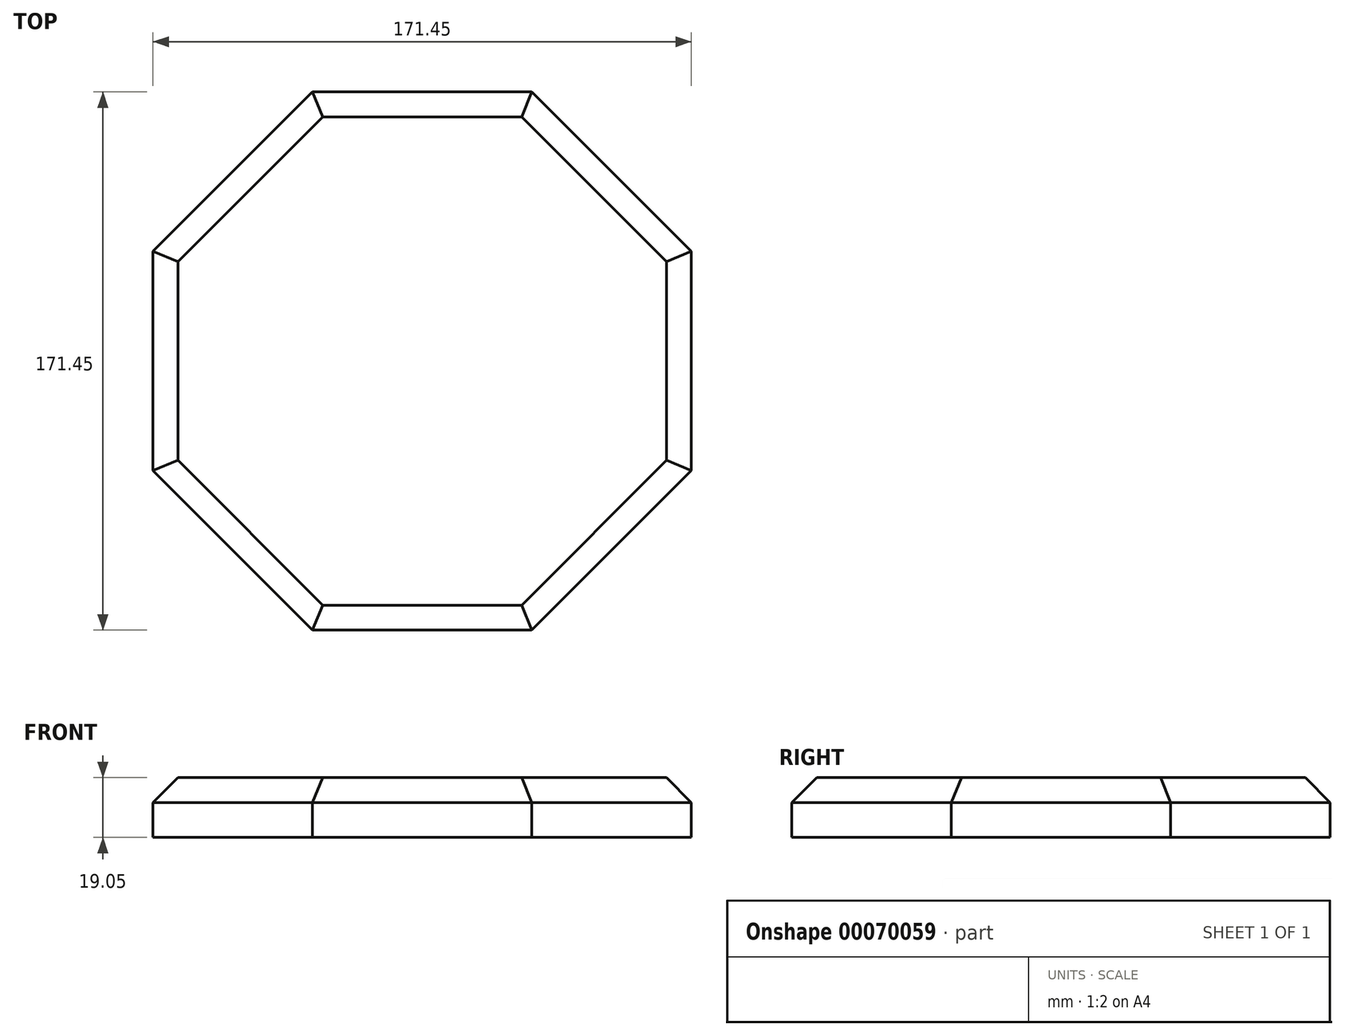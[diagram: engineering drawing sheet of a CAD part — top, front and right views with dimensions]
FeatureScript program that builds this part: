
annotation { "Feature Type Name" : "Feature", "Feature Type Description" : "" }
export const myFeature = defineFeature(function(context is Context, id is Id, definition is map)
    precondition{}
    {
        {
            var Q0;
            Q0=qCreatedBy(makeId("Top.planeOp"),FACE);
            var sketch = newSketch(context, id + "F0", { "sketchPlane" : qUnion([Q0])});
            skLineSegment(sketch, "E0.bottom", {"start": v(-85.73, 85.73) * mm, "end": v(85.73, 85.73) * mm});
            skLineSegment(sketch, "E0.top", {"start": v(-85.73, -85.73) * mm, "end": v(85.73, -85.73) * mm});
            skLineSegment(sketch, "E0.left", {"start": v(-85.73, 85.73) * mm, "end": v(-85.73, -85.73) * mm});
            skLineSegment(sketch, "E0.right", {"start": v(85.73, 85.73) * mm, "end": v(85.73, -85.73) * mm});
            skSolve(sketch);
        }
        {
            var Q0;
            Q0=makeQuery(id+"F0.imprint","IMPRINT",FACE,{"disambiguationData":[TD([[makeQuery(id+"F0.imprint","IMPRINT",EDGE,{"derivedFrom":sQuery(id+"F0.wireOp",EDGE,"E0.bottom")}),-1.0]])]});
            extrude(context, id + "F1", {"entities" : qUnion([Q0]), "depth" : 19.05 * mm});
        }
        {
            var Q0;
            Q0=makeQuery(id+"F1.opExtrude","CAP_FACE",FACE,{"disambiguationData":[OSD([sQuery(id+"F0.wireOp",EDGE,"E0.bottom"),sQuery(id+"F0.wireOp",EDGE,"E0.top"),sQuery(id+"F0.wireOp",EDGE,"E0.left"),sQuery(id+"F0.wireOp",EDGE,"E0.right"),sQuery(id+"F0.wireOp",EDGE,"989e4ac2-cbae-46ec-ac43-b30b8cb76129"),sQuery(id+"F0.wireOp",EDGE,"f01b9872-5823-4ad4-8aaf-3aa102a647f4"),sQuery(id+"F0.wireOp",EDGE,"f254082f-be6d-486d-81c3-8d4d65e6b824"),sQuery(id+"F0.wireOp",EDGE,"21b5d828-52df-4a59-b6f1-21bcb8ec3c0c"),sQuery(id+"F0.wireOp",EDGE,"d4020edf-602f-45da-a7a3-b06696fa117d"),sQuery(id+"F0.wireOp",EDGE,"905035b1-59ca-4ffc-a016-3912243c06da"),sQuery(id+"F0.wireOp",EDGE,"2c110506-1446-466a-9127-3dc12a78b58e"),sQuery(id+"F0.wireOp",EDGE,"26ce887d-3531-4269-9341-2fdd4bb3d620"),sQuery(id+"F0.wireOp",EDGE,"475ccb10-8f8e-49a7-93a4-93c3f0626b4c.bottom"),sQuery(id+"F0.wireOp",EDGE,"475ccb10-8f8e-49a7-93a4-93c3f0626b4c.top"),sQuery(id+"F0.wireOp",EDGE,"475ccb10-8f8e-49a7-93a4-93c3f0626b4c.left"),sQuery(id+"F0.wireOp",EDGE,"475ccb10-8f8e-49a7-93a4-93c3f0626b4c.right"),sQuery(id+"F0.wireOp",EDGE,"8ed021d0-fdce-44df-976c-de6f7beabc6d"),sQuery(id+"F0.wireOp",EDGE,"05c30dd9-ea8d-42c8-9be9-557685326a9e"),sQuery(id+"F0.wireOp",EDGE,"c46a8fb0-1c3f-46cc-903a-dbb448825e2e"),sQuery(id+"F0.wireOp",EDGE,"583893c2-0e6e-4aff-a0bb-19d91ca0a52e"),sQuery(id+"F0.wireOp",EDGE,"14300feb-ca35-44da-9651-15a41913f3c9.0"),sQuery(id+"F0.wireOp",EDGE,"8128e34a-8f59-4c2e-8099-998957f98d7b.0"),sQuery(id+"F0.wireOp",EDGE,"95882136-e9e6-4eb0-a4c0-31bc3ca21f6b.0"),sQuery(id+"F0.wireOp",EDGE,"ec29514e-9971-47f8-95a7-5a5ba83320e9.0")])],"isStart":false});
            var sketch = newSketch(context, id + "F2", { "sketchPlane" : qUnion([Q0])});
            skLineSegment(sketch, "E1", {"start": v(7.95, -33.34) * mm, "end": v(7.95, -20.64) * mm});
            skLineSegment(sketch, "E2", {"start": v(-33.34, 7.94) * mm, "end": v(-20.64, 7.94) * mm});
            skLineSegment(sketch, "E3", {"start": v(-20.64, -7.94) * mm, "end": v(-33.34, -7.94) * mm});
            skLineSegment(sketch, "E4", {"start": v(33.34, -9.24) * mm, "end": v(20.64, -9.24) * mm});
            skLineSegment(sketch, "E5.trimOffspring", {"start": v(-7.72, 33.34) * mm, "end": v(-7.8, 20.64) * mm});
            skPoint(sketch, "E6.center.orphan", {"position": v(0, -1.3) * mm});
            skLineSegment(sketch, "E7", {"start": v(-33.34, -7.94) * mm, "end": v(-33.34, 7.94) * mm});
            skLineSegment(sketch, "E8", {"start": v(33.34, -9.24) * mm, "end": v(33.34, 7.94) * mm});
            skPoint(sketch, "E8.startSnap0", {"position": v(33.34, -9.24) * mm});
            skLineSegment(sketch, "E9", {"start": v(-8.18, -33.34) * mm, "end": v(7.95, -33.34) * mm});
            skPoint(sketch, "E10.orphan", {"position": v(0, 20.64) * mm});
            skPoint(sketch, "E11.orphan", {"position": v(33.34, -6.04) * mm});
            skPoint(sketch, "E12.orphan", {"position": v(20.64, 0) * mm});
            skPoint(sketch, "E13.orphan", {"position": v(0, -20.64) * mm});
            skLineSegment(sketch, "E14.trimOffspring", {"start": v(20.64, 20.64) * mm, "end": v(20.64, 20.75) * mm});
            skPoint(sketch, "E15.orphan", {"position": v(-20.64, 0) * mm});
            skLineSegment(sketch, "E16.trimOffspring", {"start": v(20.75, 20.64) * mm, "end": v(20.64, 20.75) * mm});
            skLineSegment(sketch, "E17", {"start": v(-20.64, -7.94) * mm, "end": v(-8.1, -20.64) * mm});
            skLineSegment(sketch, "E18", {"start": v(20.64, -9.24) * mm, "end": v(7.95, -20.64) * mm});
            skLineSegment(sketch, "E19", {"start": v(-7.8, 20.64) * mm, "end": v(-20.64, 7.94) * mm});
            skLineSegment(sketch, "E20", {"start": v(-7.72, 33.34) * mm, "end": v(7.95, 33.34) * mm});
            skLineSegment(sketch, "E21", {"start": v(20.64, 7.94) * mm, "end": v(7.95, 20.64) * mm});
            skLineSegment(sketch, "E22.trimOffspring", {"start": v(20.64, 20.64) * mm, "end": v(20.75, 20.64) * mm});
            skLineSegment(sketch, "E23.trimOffspring", {"start": v(20.64, 7.94) * mm, "end": v(33.34, 7.94) * mm});
            skLineSegment(sketch, "E24.trimOffspring", {"start": v(-8.1, -20.64) * mm, "end": v(-8.18, -33.34) * mm});
            skLineSegment(sketch, "E25.trimOffspring", {"start": v(7.95, 20.64) * mm, "end": v(7.95, 33.34) * mm});
            skLineSegment(sketch, "E26", {"start": v(20.64, -9.24) * mm, "end": v(20.64, 7.94) * mm});
            skLineSegment(sketch, "E27", {"start": v(-20.64, -7.94) * mm, "end": v(-20.64, 7.94) * mm});
            skLineSegment(sketch, "E28", {"start": v(-7.8, 20.64) * mm, "end": v(7.95, 20.64) * mm});
            skLineSegment(sketch, "E29", {"start": v(-8.1, -20.64) * mm, "end": v(7.95, -20.64) * mm});
            skSolve(sketch);
        }
        {
            var Q0;
            Q0=makeQuery(id+"F2.imprint","IMPRINT",FACE,{"disambiguationData":[TD([[makeQuery(id+"F2.imprint","IMPRINT",EDGE,{"derivedFrom":sQuery(id+"F2.wireOp",EDGE,"E17")}),1.0]])]});
            extrude(context, id + "F3", {"entities" : qUnion([Q0]), "depth" : 127 * mm});
        }
        {
            var Q0;
            Q0=makeQuery(id+"F2.imprint","IMPRINT",FACE,{"disambiguationData":[TD([[makeQuery(id+"F2.imprint","IMPRINT",EDGE,{"derivedFrom":sQuery(id+"F2.wireOp",EDGE,"E4")}),-1.0]])]});
            extrude(context, id + "F4", {"entities" : qUnion([Q0]), "depth" : 203.2 * mm});
        }
        {
            var Q0;
            Q0=makeQuery(id+"F4.opExtrude","CAP_EDGE",EDGE,{"disambiguationData":[OSD([sQuery(id+"F2.wireOp",EDGE,"E8")])],"isStart":false});
            chamfer(context, id + "F5", {"entities" : qUnion([Q0]), "width" : 5.08 * mm, "tangentPropagation" : true});
        }
        {
            var Q0;
            Q0=makeQuery(id+"F2.imprint","IMPRINT",FACE,{"disambiguationData":[TD([[makeQuery(id+"F2.imprint","IMPRINT",EDGE,{"derivedFrom":sQuery(id+"F2.wireOp",EDGE,"E1")}),1.0]])]});
            extrude(context, id + "F6", {"entities" : qUnion([Q0]), "depth" : 177.8 * mm});
        }
        {
            var Q0;
            Q0=makeQuery(id+"F6.opExtrude","CAP_EDGE",EDGE,{"disambiguationData":[OSD([sQuery(id+"F2.wireOp",EDGE,"E9")])],"isStart":false});
            chamfer(context, id + "F7", {"entities" : qUnion([Q0]), "width" : 5.08 * mm, "tangentPropagation" : true});
        }
        {
            var Q0;
            Q0=makeQuery(id+"F2.imprint","IMPRINT",FACE,{"disambiguationData":[TD([[makeQuery(id+"F2.imprint","IMPRINT",EDGE,{"derivedFrom":sQuery(id+"F2.wireOp",EDGE,"E5.trimOffspring")}),1.0]])]});
            extrude(context, id + "F8", {"entities" : qUnion([Q0]), "depth" : 177.8 * mm});
        }
        {
            var Q0;
            Q0=makeQuery(id+"F8.opExtrude","CAP_EDGE",EDGE,{"disambiguationData":[OSD([sQuery(id+"F2.wireOp",EDGE,"E20")])],"isStart":false});
            chamfer(context, id + "F9", {"entities" : qUnion([Q0]), "width" : 5.08 * mm, "tangentPropagation" : true});
        }
        {
            var Q0;
            Q0=makeQuery(id+"F2.imprint","IMPRINT",FACE,{"disambiguationData":[TD([[makeQuery(id+"F2.imprint","IMPRINT",EDGE,{"derivedFrom":sQuery(id+"F2.wireOp",EDGE,"E2")}),-1.0]])]});
            extrude(context, id + "F10", {"entities" : qUnion([Q0]), "depth" : 152.4 * mm});
        }
        {
            var Q0;
            Q0=makeQuery(id+"F10.opExtrude","CAP_EDGE",EDGE,{"disambiguationData":[OSD([sQuery(id+"F2.wireOp",EDGE,"E7")])],"isStart":false});
            chamfer(context, id + "F11", {"entities" : qUnion([Q0]), "width" : 5.08 * mm, "tangentPropagation" : true});
        }
        {
            var Q0;
            Q0=makeQuery(id+"F1.opExtrude","SWEPT_EDGE",EDGE,{"disambiguationData":[OSD([sQuery(id+"F0.wireOp",EDGE,"E0.bottom"),sQuery(id+"F0.wireOp",EDGE,"E0.right")])]});
            var Q1;
            Q1=makeQuery(id+"F1.opExtrude","SWEPT_EDGE",EDGE,{"disambiguationData":[OSD([sQuery(id+"F0.wireOp",EDGE,"E0.bottom"),sQuery(id+"F0.wireOp",EDGE,"E0.left")])]});
            var Q2;
            Q2=makeQuery(id+"F1.opExtrude","SWEPT_EDGE",EDGE,{"disambiguationData":[OSD([sQuery(id+"F0.wireOp",EDGE,"E0.top"),sQuery(id+"F0.wireOp",EDGE,"E0.right")])]});
            var Q3;
            Q3=makeQuery(id+"F1.opExtrude","SWEPT_EDGE",EDGE,{"disambiguationData":[OSD([sQuery(id+"F0.wireOp",EDGE,"E0.top"),sQuery(id+"F0.wireOp",EDGE,"E0.left")])]});
            chamfer(context, id + "F12", {"entities" : qUnion([Q0, Q1, Q2, Q3]), "width" : 50.8 * mm, "tangentPropagation" : true});
        }
        {
            var Q0;
            {var subQ0=sQuery(id+"F0.wireOp",EDGE,"E0.left");var subQ1=sQuery(id+"F0.wireOp",EDGE,"E0.top");Q0=makeQuery(id+"F12.opChamfer","BLEND_EDGE",EDGE,{"blendedFrom":[makeQuery(id+"F1.opExtrude","SWEPT_EDGE",EDGE,{"disambiguationData":[OSD([subQ1,subQ0])]}),makeQuery(id+"F1.opExtrude","CAP_FACE",FACE,{"disambiguationData":[OSD([sQuery(id+"F0.wireOp",EDGE,"E0.bottom"),subQ1,subQ0,sQuery(id+"F0.wireOp",EDGE,"E0.right")])],"isStart":false})],"blendedInto":[makeQuery(id+"F1.opExtrude","CAP_FACE",FACE,{"disambiguationData":[OSD([sQuery(id+"F0.wireOp",EDGE,"E0.bottom"),subQ1,subQ0,sQuery(id+"F0.wireOp",EDGE,"E0.right")])],"isStart":false})]});}
            var Q1;
            Q1=makeQuery(id+"F1.opExtrude","CAP_EDGE",EDGE,{"disambiguationData":[OSD([sQuery(id+"F0.wireOp",EDGE,"E0.top")])],"isStart":false});
            var Q2;
            {var subQ0=sQuery(id+"F0.wireOp",EDGE,"E0.right");var subQ1=sQuery(id+"F0.wireOp",EDGE,"E0.top");Q2=makeQuery(id+"F12.opChamfer","BLEND_EDGE",EDGE,{"blendedFrom":[makeQuery(id+"F1.opExtrude","SWEPT_EDGE",EDGE,{"disambiguationData":[OSD([subQ1,subQ0])]}),makeQuery(id+"F1.opExtrude","CAP_FACE",FACE,{"disambiguationData":[OSD([sQuery(id+"F0.wireOp",EDGE,"E0.bottom"),subQ1,sQuery(id+"F0.wireOp",EDGE,"E0.left"),subQ0])],"isStart":false})],"blendedInto":[makeQuery(id+"F1.opExtrude","CAP_FACE",FACE,{"disambiguationData":[OSD([sQuery(id+"F0.wireOp",EDGE,"E0.bottom"),subQ1,sQuery(id+"F0.wireOp",EDGE,"E0.left"),subQ0])],"isStart":false})]});}
            var Q3;
            Q3=makeQuery(id+"F1.opExtrude","CAP_EDGE",EDGE,{"disambiguationData":[OSD([sQuery(id+"F0.wireOp",EDGE,"E0.right")])],"isStart":false});
            var Q4;
            {var subQ0=sQuery(id+"F0.wireOp",EDGE,"E0.right");var subQ1=sQuery(id+"F0.wireOp",EDGE,"E0.bottom");Q4=makeQuery(id+"F12.opChamfer","BLEND_EDGE",EDGE,{"blendedFrom":[makeQuery(id+"F1.opExtrude","SWEPT_EDGE",EDGE,{"disambiguationData":[OSD([subQ1,subQ0])]}),makeQuery(id+"F1.opExtrude","CAP_FACE",FACE,{"disambiguationData":[OSD([subQ1,sQuery(id+"F0.wireOp",EDGE,"E0.top"),sQuery(id+"F0.wireOp",EDGE,"E0.left"),subQ0])],"isStart":false})],"blendedInto":[makeQuery(id+"F1.opExtrude","CAP_FACE",FACE,{"disambiguationData":[OSD([subQ1,sQuery(id+"F0.wireOp",EDGE,"E0.top"),sQuery(id+"F0.wireOp",EDGE,"E0.left"),subQ0])],"isStart":false})]});}
            var Q5;
            Q5=makeQuery(id+"F1.opExtrude","CAP_EDGE",EDGE,{"disambiguationData":[OSD([sQuery(id+"F0.wireOp",EDGE,"E0.bottom")])],"isStart":false});
            var Q6;
            {var subQ0=sQuery(id+"F0.wireOp",EDGE,"E0.left");var subQ1=sQuery(id+"F0.wireOp",EDGE,"E0.bottom");Q6=makeQuery(id+"F12.opChamfer","BLEND_EDGE",EDGE,{"blendedFrom":[makeQuery(id+"F1.opExtrude","SWEPT_EDGE",EDGE,{"disambiguationData":[OSD([subQ1,subQ0])]}),makeQuery(id+"F1.opExtrude","CAP_FACE",FACE,{"disambiguationData":[OSD([subQ1,sQuery(id+"F0.wireOp",EDGE,"E0.top"),subQ0,sQuery(id+"F0.wireOp",EDGE,"E0.right")])],"isStart":false})],"blendedInto":[makeQuery(id+"F1.opExtrude","CAP_FACE",FACE,{"disambiguationData":[OSD([subQ1,sQuery(id+"F0.wireOp",EDGE,"E0.top"),subQ0,sQuery(id+"F0.wireOp",EDGE,"E0.right")])],"isStart":false})]});}
            var Q7;
            Q7=makeQuery(id+"F1.opExtrude","CAP_EDGE",EDGE,{"disambiguationData":[OSD([sQuery(id+"F0.wireOp",EDGE,"E0.left")])],"isStart":false});
            chamfer(context, id + "F13", {"entities" : qUnion([Q0, Q1, Q2, Q3, Q4, Q5, Q6, Q7]), "width" : 7.94 * mm, "tangentPropagation" : true});
        }
        {
            var Q0;
            Q0=makeQuery(id+"F3.opExtrude","CAP_FACE",FACE,{"disambiguationData":[OSD([sQuery(id+"F2.wireOp",EDGE,"E17"),sQuery(id+"F2.wireOp",EDGE,"E18"),sQuery(id+"F2.wireOp",EDGE,"E19"),sQuery(id+"F2.wireOp",EDGE,"E21"),sQuery(id+"F2.wireOp",EDGE,"E26"),sQuery(id+"F2.wireOp",EDGE,"E27"),sQuery(id+"F2.wireOp",EDGE,"E28"),sQuery(id+"F2.wireOp",EDGE,"E29")])],"isStart":false});
            var sketch = newSketch(context, id + "F14", { "sketchPlane" : qUnion([Q0])});
            skCircle(sketch, "E30", {"center": v(0, 0) * mm, "radius": 20.66 * mm});
            skSolve(sketch);
        }
        {
            var Q0;
            {var subQ0=sQuery(id+"F14.wireOp",EDGE,"E30");var subQ9=makeQuery(id+"F3.opExtrude","CAP_EDGE",EDGE,{"disambiguationData":[OSD([sQuery(id+"F2.wireOp",EDGE,"E21")])],"isStart":false});var subQ10=makeQuery(id+"F14.imprint","INTERSECT",VERTEX,{"disambiguationData":[OD(0.0)],"derivedFrom":[subQ9,subQ0]});Q0=makeQuery(id+"F14.imprint","IMPRINT",FACE,{"disambiguationData":[TD([[makeQuery(id+"F14.imprint","IMPRINT",EDGE,{"disambiguationData":[TD([[subQ10,1.0]])],"derivedFrom":subQ0}),1.0]])]});}
            var sketch = newSketch(context, id + "F15", { "sketchPlane" : qUnion([Q0])});
            skCircle(sketch, "E31", {"center": v(0, 0) * mm, "radius": 19.81 * mm});
            skSolve(sketch);
        }
        {
            var Q0;
            Q0=qSketchRegion(id+"F15",true);
            extrude(context, id + "F16", {"entities" : qUnion([Q0]), "depth" : 355.6 * mm});
        }
        {
            var Q0;
            Q0=makeQuery(id+"F16.opExtrude","CAP_EDGE",EDGE,{"disambiguationData":[OSD([sQuery(id+"F15.wireOp",EDGE,"E31")])],"isStart":false});
            chamfer(context, id + "F17", {"entities" : qUnion([Q0]), "width" : 5.08 * mm, "tangentPropagation" : true});
        }
        {
            var Q0;
            {var subQ0=sQuery(id+"F14.wireOp",EDGE,"E30");var subQ9=makeQuery(id+"F3.opExtrude","CAP_EDGE",EDGE,{"disambiguationData":[OSD([sQuery(id+"F2.wireOp",EDGE,"E21")])],"isStart":false});var subQ10=makeQuery(id+"F14.imprint","INTERSECT",VERTEX,{"disambiguationData":[OD(0.0)],"derivedFrom":[subQ9,subQ0]});Q0=makeQuery(id+"F14.imprint","IMPRINT",FACE,{"disambiguationData":[TD([[makeQuery(id+"F14.imprint","IMPRINT",EDGE,{"disambiguationData":[TD([[subQ10,1.0]])],"derivedFrom":subQ0}),1.0]])]});}
            extrude(context, id + "F18", {"entities" : qUnion([Q0]), "depth" : 25.4 * mm});
        }
        {
            var Q0;
            Q0=makeQuery(id+"F16.opExtrude","SWEPT_BODY",BODY,{"disambiguationData":[OSD([sQuery(id+"F15.wireOp",EDGE,"E31")])]});
            deleteBodies(context, id + "F19", {"entities" : qUnion([Q0])});
        }
        {
            var Q0;
            Q0=makeQuery(id+"F4.opExtrude","SWEPT_BODY",BODY,{"disambiguationData":[OSD([sQuery(id+"F2.wireOp",EDGE,"E4"),sQuery(id+"F2.wireOp",EDGE,"E8"),sQuery(id+"F2.wireOp",EDGE,"E23.trimOffspring"),sQuery(id+"F2.wireOp",EDGE,"E26")])]});
            deleteBodies(context, id + "F20", {"entities" : qUnion([Q0])});
        }
        {
            var Q0;
            Q0=makeQuery(id+"F3.opExtrude","SWEPT_BODY",BODY,{"disambiguationData":[OSD([sQuery(id+"F2.wireOp",EDGE,"E17"),sQuery(id+"F2.wireOp",EDGE,"E18"),sQuery(id+"F2.wireOp",EDGE,"E19"),sQuery(id+"F2.wireOp",EDGE,"E21"),sQuery(id+"F2.wireOp",EDGE,"E26"),sQuery(id+"F2.wireOp",EDGE,"E27"),sQuery(id+"F2.wireOp",EDGE,"E28"),sQuery(id+"F2.wireOp",EDGE,"E29")])]});
            deleteBodies(context, id + "F21", {"entities" : qUnion([Q0])});
        }
        {
            var Q0;
            Q0=makeQuery(id+"F18.opExtrude","SWEPT_BODY",BODY,{"disambiguationData":[OSD([sQuery(id+"F2.wireOp",EDGE,"E17"),sQuery(id+"F2.wireOp",EDGE,"E19"),sQuery(id+"F2.wireOp",EDGE,"E21"),sQuery(id+"F2.wireOp",EDGE,"E26"),sQuery(id+"F2.wireOp",EDGE,"E27"),sQuery(id+"F2.wireOp",EDGE,"E28"),sQuery(id+"F2.wireOp",EDGE,"E29"),sQuery(id+"F14.wireOp",EDGE,"E30")])]});
            deleteBodies(context, id + "F22", {"entities" : qUnion([Q0])});
        }
        {
            var Q0;
            Q0=makeQuery(id+"F8.opExtrude","SWEPT_BODY",BODY,{"disambiguationData":[OSD([sQuery(id+"F2.wireOp",EDGE,"E5.trimOffspring"),sQuery(id+"F2.wireOp",EDGE,"E20"),sQuery(id+"F2.wireOp",EDGE,"E25.trimOffspring"),sQuery(id+"F2.wireOp",EDGE,"E28")])]});
            deleteBodies(context, id + "F23", {"entities" : qUnion([Q0])});
        }
        {
            var Q0;
            Q0=makeQuery(id+"F6.opExtrude","SWEPT_BODY",BODY,{"disambiguationData":[OSD([sQuery(id+"F2.wireOp",EDGE,"E1"),sQuery(id+"F2.wireOp",EDGE,"E9"),sQuery(id+"F2.wireOp",EDGE,"E24.trimOffspring"),sQuery(id+"F2.wireOp",EDGE,"E29")])]});
            deleteBodies(context, id + "F24", {"entities" : qUnion([Q0])});
        }
        {
            var Q0;
            Q0=makeQuery(id+"F10.opExtrude","SWEPT_BODY",BODY,{"disambiguationData":[OSD([sQuery(id+"F2.wireOp",EDGE,"E2"),sQuery(id+"F2.wireOp",EDGE,"E3"),sQuery(id+"F2.wireOp",EDGE,"E7"),sQuery(id+"F2.wireOp",EDGE,"E27")])]});
            deleteBodies(context, id + "F25", {"entities" : qUnion([Q0])});
        }
    });
